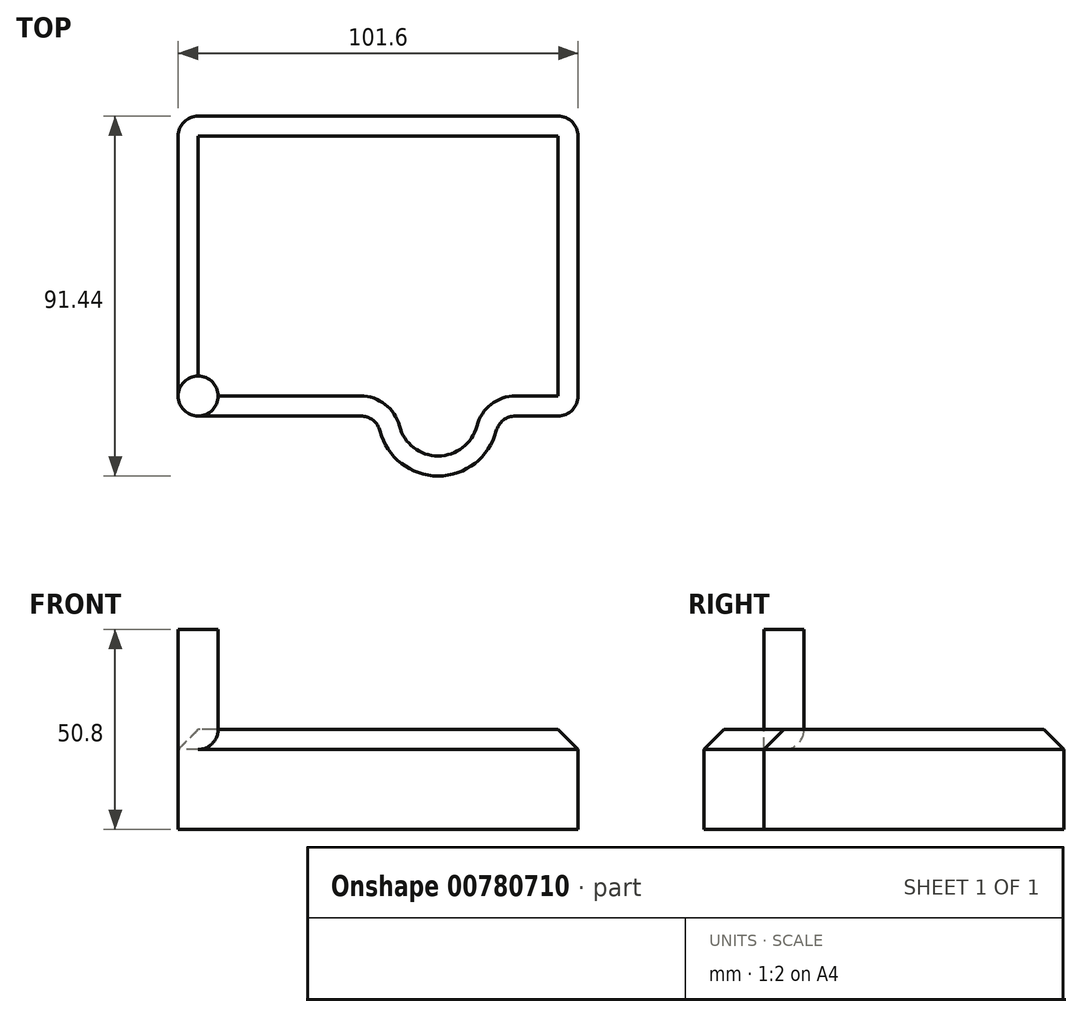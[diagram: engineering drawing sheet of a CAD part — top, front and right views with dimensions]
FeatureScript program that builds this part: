
annotation { "Feature Type Name" : "Feature", "Feature Type Description" : "" }
export const myFeature = defineFeature(function(context is Context, id is Id, definition is map)
    precondition{}
    {
        {
            var Q0;
            Q0=qCreatedBy(makeId("Top.planeOp"),FACE);
            var sketch = newSketch(context, id + "F0", { "sketchPlane" : qUnion([Q0])});
            skLineSegment(sketch, "E0.bottom", {"start": v(0, 0) * mm, "end": v(50.8, 0) * mm});
            skLineSegment(sketch, "E0.top", {"start": v(0, 76.2) * mm, "end": v(101.6, 76.2) * mm});
            skLineSegment(sketch, "E0.left", {"start": v(0, 0) * mm, "end": v(0, 76.2) * mm});
            skLineSegment(sketch, "E0.right", {"start": v(101.6, 0) * mm, "end": v(101.6, 76.2) * mm});
            skArc(sketch, "E1", {"start": v(50.8, 0) * mm, "mid": v(66.04, -15.24) * mm, "end": v(81.28, 0) * mm});
            skLineSegment(sketch, "E2.trimOffspring", {"start": v(81.28, 0) * mm, "end": v(101.6, 0) * mm});
            skLineSegment(sketch, "E3", {"start": v(50.8, 0) * mm, "end": v(81.28, 0) * mm, "construction": true});
            skSolve(sketch);
        }
        {
            var Q0;
            Q0=makeQuery(id+"F0.imprint","IMPRINT",FACE,{"disambiguationData":[TD([[makeQuery(id+"F0.imprint","IMPRINT",EDGE,{"derivedFrom":sQuery(id+"F0.wireOp",EDGE,"E0.bottom")}),1.0]])]});
            extrude(context, id + "F1", {"entities" : qUnion([Q0]), "depth" : 25.4 * mm, "offsetDistance" : 25.4 * mm});
        }
        {
            var Q0;
            Q0=makeQuery(id+"F1.opExtrude","SWEPT_EDGE",EDGE,{"disambiguationData":[OSD([sQuery(id+"F0.wireOp",EDGE,"E0.top"),sQuery(id+"F0.wireOp",EDGE,"E0.left")])]});
            var Q1;
            Q1=makeQuery(id+"F1.opExtrude","SWEPT_EDGE",EDGE,{"disambiguationData":[OSD([sQuery(id+"F0.wireOp",EDGE,"E0.bottom"),sQuery(id+"F0.wireOp",EDGE,"E0.left")])]});
            var Q2;
            Q2=makeQuery(id+"F1.opExtrude","SWEPT_EDGE",EDGE,{"disambiguationData":[OSD([sQuery(id+"F0.wireOp",EDGE,"E1"),sQuery(id+"F0.wireOp",EDGE,"E2.trimOffspring")])]});
            var Q3;
            Q3=makeQuery(id+"F1.opExtrude","SWEPT_EDGE",EDGE,{"disambiguationData":[OSD([sQuery(id+"F0.wireOp",EDGE,"E0.right"),sQuery(id+"F0.wireOp",EDGE,"E2.trimOffspring")])]});
            var Q4;
            Q4=makeQuery(id+"F1.opExtrude","SWEPT_EDGE",EDGE,{"disambiguationData":[OSD([sQuery(id+"F0.wireOp",EDGE,"E0.top"),sQuery(id+"F0.wireOp",EDGE,"E0.right")])]});
            var Q5;
            Q5=makeQuery(id+"F1.opExtrude","SWEPT_EDGE",EDGE,{"disambiguationData":[OSD([sQuery(id+"F0.wireOp",EDGE,"E0.bottom"),sQuery(id+"F0.wireOp",EDGE,"E1")])]});
            fillet(context, id + "F2", {"entities" : qUnion([Q0, Q1, Q2, Q3, Q4, Q5]), "radius" : 5.08 * mm, "tangentPropagation" : true, "allowEdgeOverflow" : false});
        }
        {
            var Q0;
            Q0=makeQuery(id+"F1.opExtrude","CAP_FACE",FACE,{"disambiguationData":[OSD([sQuery(id+"F0.wireOp",EDGE,"E0.bottom"),sQuery(id+"F0.wireOp",EDGE,"E0.top"),sQuery(id+"F0.wireOp",EDGE,"E0.left"),sQuery(id+"F0.wireOp",EDGE,"E0.right"),sQuery(id+"F0.wireOp",EDGE,"E1"),sQuery(id+"F0.wireOp",EDGE,"E2.trimOffspring")])],"isStart":false});
            var sketch = newSketch(context, id + "F3", { "sketchPlane" : qUnion([Q0])});
            skCircle(sketch, "E4", {"center": v(5.08, 5.08) * mm, "radius": 5.08 * mm});
            skSolve(sketch);
        }
        {
            var Q0;
            {var subQ0=sQuery(id+"F3.wireOp",EDGE,"E4");var subQ1=makeQuery(id+"F3.imprint","INTERSECT",VERTEX,{"derivedFrom":[makeQuery(id+"F1.opExtrude","CAP_EDGE",EDGE,{"disambiguationData":[OSD([sQuery(id+"F0.wireOp",EDGE,"E0.bottom")])],"isStart":false}),subQ0]});Q0=makeQuery(id+"F3.imprint","IMPRINT",FACE,{"disambiguationData":[TD([[makeQuery(id+"F3.imprint","IMPRINT",EDGE,{"disambiguationData":[TD([[subQ1,1.0]])],"derivedFrom":subQ0}),1.0]])]});}
            extrude(context, id + "F4", {"entities" : qUnion([Q0]), "operationType" : NewBodyOperationType.ADD, "depth" : 25.4 * mm, "offsetDistance" : 25.4 * mm});
        }
        {
            var Q0;
            Q0=makeQuery(id+"F1.opExtrude","CAP_EDGE",EDGE,{"disambiguationData":[OSD([sQuery(id+"F0.wireOp",EDGE,"E0.bottom")])],"isStart":false});
            chamfer(context, id + "F5", {"entities" : qUnion([Q0]), "width" : 5.08 * mm, "tangentPropagation" : true});
        }
    });
